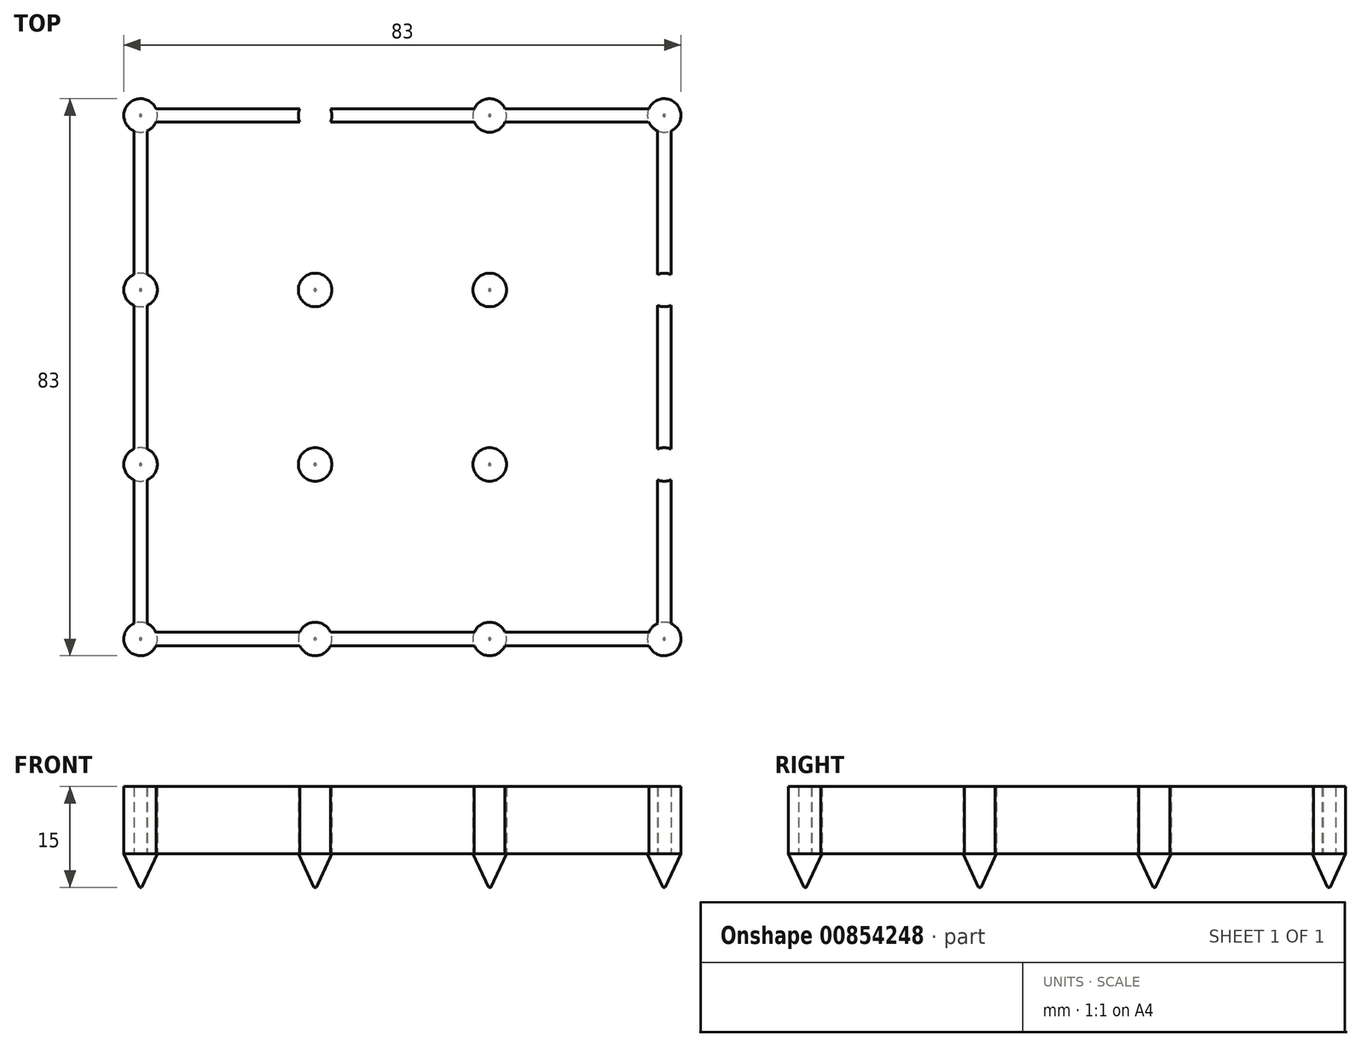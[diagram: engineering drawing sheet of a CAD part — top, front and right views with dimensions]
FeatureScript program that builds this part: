
annotation { "Feature Type Name" : "Feature", "Feature Type Description" : "" }
export const myFeature = defineFeature(function(context is Context, id is Id, definition is map)
    precondition{}
    {
        {
            var Q0;
            Q0=qCreatedBy(makeId("Top.planeOp"),FACE);
            var sketch = newSketch(context, id + "F0", { "sketchPlane" : qUnion([Q0])});
            skLineSegment(sketch, "E0.bottom", {"start": v(13, 13) * mm, "end": v(-13, 13) * mm, "construction": true});
            skLineSegment(sketch, "E0.top", {"start": v(13, -13) * mm, "end": v(-13, -13) * mm, "construction": true});
            skLineSegment(sketch, "E0.left", {"start": v(13, 13) * mm, "end": v(13, -13) * mm, "construction": true});
            skLineSegment(sketch, "E0.right", {"start": v(-13, 13) * mm, "end": v(-13, -13) * mm, "construction": true});
            skPoint(sketch, "E0.middle", {"position": v(0, 0) * mm});
            skCircle(sketch, "E1", {"center": v(13, 13) * mm, "radius": 2.5 * mm});
            skCircle(sketch, "E2", {"center": v(-13, 13) * mm, "radius": 2.5 * mm});
            skCircle(sketch, "E3", {"center": v(-13, -13) * mm, "radius": 2.5 * mm});
            skCircle(sketch, "E4", {"center": v(13, -13) * mm, "radius": 2.5 * mm});
            skLineSegment(sketch, "E5", {"start": v(-14, 10.7) * mm, "end": v(-14, -10.7) * mm});
            skLineSegment(sketch, "E6", {"start": v(-12, 10.7) * mm, "end": v(-12, -10.7) * mm});
            skLineSegment(sketch, "E7", {"start": v(-10.7, 14) * mm, "end": v(10.7, 14) * mm});
            skLineSegment(sketch, "E8", {"start": v(-10.7, 12) * mm, "end": v(10.7, 12) * mm});
            skLineSegment(sketch, "E9", {"start": v(12, 10.7) * mm, "end": v(12, -10.7) * mm});
            skLineSegment(sketch, "E10", {"start": v(14, 10.7) * mm, "end": v(14, -10.7) * mm});
            skLineSegment(sketch, "E11", {"start": v(-10.7, -12) * mm, "end": v(10.7, -12) * mm});
            skLineSegment(sketch, "E12", {"start": v(-10.7, -14) * mm, "end": v(10.7, -14) * mm});
            skLineSegment(sketch, "E13.0.1.1", {"start": v(14, 36.7) * mm, "end": v(14, 15.3) * mm});
            skLineSegment(sketch, "E13.0.1.4", {"start": v(-14, 36.7) * mm, "end": v(-14, 15.3) * mm});
            skLineSegment(sketch, "E13.0.1.5", {"start": v(13, 39) * mm, "end": v(13, 13) * mm, "construction": true});
            skLineSegment(sketch, "E13.0.1.6", {"start": v(-10.7, 40) * mm, "end": v(10.7, 40) * mm});
            skLineSegment(sketch, "E13.0.1.7", {"start": v(13, 39) * mm, "end": v(-13, 39) * mm, "construction": true});
            skLineSegment(sketch, "E13.0.1.8", {"start": v(12, 36.7) * mm, "end": v(12, 15.3) * mm});
            skLineSegment(sketch, "E13.0.1.9", {"start": v(-13, 39) * mm, "end": v(-13, 13) * mm, "construction": true});
            skLineSegment(sketch, "E13.0.1.10", {"start": v(-12, 36.7) * mm, "end": v(-12, 15.3) * mm});
            skLineSegment(sketch, "E13.0.1.11", {"start": v(-10.7, 38) * mm, "end": v(10.7, 38) * mm});
            skPoint(sketch, "E13.0.1.12", {"position": v(0, 26) * mm});
            skCircle(sketch, "E13.0.1.15", {"center": v(13, 39) * mm, "radius": 2.5 * mm});
            skCircle(sketch, "E13.0.1.16", {"center": v(-13, 39) * mm, "radius": 2.5 * mm});
            skLineSegment(sketch, "E13.1.0.0", {"start": v(15.3, -12) * mm, "end": v(36.7, -12) * mm});
            skLineSegment(sketch, "E13.1.0.1", {"start": v(40, 10.7) * mm, "end": v(40, -10.7) * mm});
            skLineSegment(sketch, "E13.1.0.2", {"start": v(15.3, -14) * mm, "end": v(36.7, -14) * mm});
            skLineSegment(sketch, "E13.1.0.3", {"start": v(39, -13) * mm, "end": v(13, -13) * mm, "construction": true});
            skLineSegment(sketch, "E13.1.0.5", {"start": v(39, 13) * mm, "end": v(39, -13) * mm, "construction": true});
            skLineSegment(sketch, "E13.1.0.6", {"start": v(15.3, 14) * mm, "end": v(36.7, 14) * mm});
            skLineSegment(sketch, "E13.1.0.7", {"start": v(39, 13) * mm, "end": v(13, 13) * mm, "construction": true});
            skLineSegment(sketch, "E13.1.0.8", {"start": v(38, 10.7) * mm, "end": v(38, -10.7) * mm});
            skLineSegment(sketch, "E13.1.0.11", {"start": v(15.3, 12) * mm, "end": v(36.7, 12) * mm});
            skPoint(sketch, "E13.1.0.12", {"position": v(26, 0) * mm});
            skCircle(sketch, "E13.1.0.14", {"center": v(39, -13) * mm, "radius": 2.5 * mm});
            skCircle(sketch, "E13.1.0.15", {"center": v(39, 13) * mm, "radius": 2.5 * mm});
            skLineSegment(sketch, "E13.1.1.0", {"start": v(15.3, 14) * mm, "end": v(36.7, 14) * mm});
            skLineSegment(sketch, "E13.1.1.1", {"start": v(40, 36.7) * mm, "end": v(40, 15.3) * mm});
            skLineSegment(sketch, "E13.1.1.2", {"start": v(15.3, 12) * mm, "end": v(36.7, 12) * mm});
            skLineSegment(sketch, "E13.1.1.3", {"start": v(39, 13) * mm, "end": v(13, 13) * mm, "construction": true});
            skLineSegment(sketch, "E13.1.1.4", {"start": v(12, 36.7) * mm, "end": v(12, 15.3) * mm});
            skLineSegment(sketch, "E13.1.1.5", {"start": v(39, 39) * mm, "end": v(39, 13) * mm, "construction": true});
            skLineSegment(sketch, "E13.1.1.6", {"start": v(15.3, 40) * mm, "end": v(36.7, 40) * mm});
            skLineSegment(sketch, "E13.1.1.7", {"start": v(39, 39) * mm, "end": v(13, 39) * mm, "construction": true});
            skLineSegment(sketch, "E13.1.1.8", {"start": v(38, 36.7) * mm, "end": v(38, 15.3) * mm});
            skLineSegment(sketch, "E13.1.1.9", {"start": v(13, 39) * mm, "end": v(13, 13) * mm, "construction": true});
            skLineSegment(sketch, "E13.1.1.10", {"start": v(14, 36.7) * mm, "end": v(14, 15.3) * mm});
            skLineSegment(sketch, "E13.1.1.11", {"start": v(15.3, 38) * mm, "end": v(36.7, 38) * mm});
            skPoint(sketch, "E13.1.1.12", {"position": v(26, 26) * mm});
            skCircle(sketch, "E13.1.1.14", {"center": v(39, 13) * mm, "radius": 2.5 * mm});
            skCircle(sketch, "E13.1.1.15", {"center": v(39, 39) * mm, "radius": 2.5 * mm});
            skCircle(sketch, "E13.1.1.16", {"center": v(13, 39) * mm, "radius": 2.5 * mm});
            skLineSegment(sketch, "E13.direction1", {"start": v(-13, -13) * mm, "end": v(13, -13) * mm, "construction": true});
            skLineSegment(sketch, "E13.direction2", {"start": v(-13, -13) * mm, "end": v(-13, 13) * mm, "construction": true});
            skLineSegment(sketch, "E14.3.0.2", {"start": v(14, 62.7) * mm, "end": v(14, 41.3) * mm});
            skLineSegment(sketch, "E14.12.0.2", {"start": v(-14, 62.7) * mm, "end": v(-14, 41.3) * mm});
            skLineSegment(sketch, "E14.15.0.2", {"start": v(13, 65) * mm, "end": v(13, 39) * mm, "construction": true});
            skLineSegment(sketch, "E14.18.0.2", {"start": v(-10.7, 66) * mm, "end": v(10.7, 66) * mm});
            skLineSegment(sketch, "E14.21.0.2", {"start": v(13, 65) * mm, "end": v(-13, 65) * mm, "construction": true});
            skLineSegment(sketch, "E14.24.0.2", {"start": v(12, 62.7) * mm, "end": v(12, 41.3) * mm});
            skLineSegment(sketch, "E14.27.0.2", {"start": v(-13, 65) * mm, "end": v(-13, 39) * mm, "construction": true});
            skLineSegment(sketch, "E14.30.0.2", {"start": v(-12, 62.7) * mm, "end": v(-12, 41.3) * mm});
            skLineSegment(sketch, "E14.33.0.2", {"start": v(-10.7, 64) * mm, "end": v(10.7, 64) * mm});
            skPoint(sketch, "E14.36.0.2", {"position": v(0, 52) * mm});
            skCircle(sketch, "E14.41.0.2", {"center": v(13, 65) * mm, "radius": 2.5 * mm});
            skCircle(sketch, "E14.43.0.2", {"center": v(-13, 65) * mm, "radius": 2.5 * mm});
            skLineSegment(sketch, "E14.3.1.2", {"start": v(40, 62.7) * mm, "end": v(40, 41.3) * mm});
            skLineSegment(sketch, "E14.12.1.2", {"start": v(12, 62.7) * mm, "end": v(12, 41.3) * mm});
            skLineSegment(sketch, "E14.15.1.2", {"start": v(39, 65) * mm, "end": v(39, 39) * mm, "construction": true});
            skLineSegment(sketch, "E14.18.1.2", {"start": v(15.3, 66) * mm, "end": v(36.7, 66) * mm});
            skLineSegment(sketch, "E14.21.1.2", {"start": v(39, 65) * mm, "end": v(13, 65) * mm, "construction": true});
            skLineSegment(sketch, "E14.24.1.2", {"start": v(38, 62.7) * mm, "end": v(38, 41.3) * mm});
            skLineSegment(sketch, "E14.27.1.2", {"start": v(13, 65) * mm, "end": v(13, 39) * mm, "construction": true});
            skLineSegment(sketch, "E14.30.1.2", {"start": v(14, 62.7) * mm, "end": v(14, 41.3) * mm});
            skLineSegment(sketch, "E14.33.1.2", {"start": v(15.3, 64) * mm, "end": v(36.7, 64) * mm});
            skPoint(sketch, "E14.36.1.2", {"position": v(26, 52) * mm});
            skCircle(sketch, "E14.41.1.2", {"center": v(39, 65) * mm, "radius": 2.5 * mm});
            skCircle(sketch, "E14.43.1.2", {"center": v(13, 65) * mm, "radius": 2.5 * mm});
            skLineSegment(sketch, "E15.0.2.0", {"start": v(41.3, -12) * mm, "end": v(62.7, -12) * mm});
            skLineSegment(sketch, "E15.3.2.0", {"start": v(66, 10.7) * mm, "end": v(66, -10.7) * mm});
            skLineSegment(sketch, "E15.6.2.0", {"start": v(41.3, -14) * mm, "end": v(62.7, -14) * mm});
            skLineSegment(sketch, "E15.9.2.0", {"start": v(65, -13) * mm, "end": v(39, -13) * mm, "construction": true});
            skLineSegment(sketch, "E15.15.2.0", {"start": v(65, 13) * mm, "end": v(65, -13) * mm, "construction": true});
            skLineSegment(sketch, "E15.18.2.0", {"start": v(41.3, 14) * mm, "end": v(62.7, 14) * mm});
            skLineSegment(sketch, "E15.21.2.0", {"start": v(65, 13) * mm, "end": v(39, 13) * mm, "construction": true});
            skLineSegment(sketch, "E15.24.2.0", {"start": v(64, 10.7) * mm, "end": v(64, -10.7) * mm});
            skLineSegment(sketch, "E15.33.2.0", {"start": v(41.3, 12) * mm, "end": v(62.7, 12) * mm});
            skPoint(sketch, "E15.36.2.0", {"position": v(52, 0) * mm});
            skCircle(sketch, "E15.39.2.0", {"center": v(65, -13) * mm, "radius": 2.5 * mm});
            skCircle(sketch, "E15.41.2.0", {"center": v(65, 13) * mm, "radius": 2.5 * mm});
            skLineSegment(sketch, "E15.0.2.1", {"start": v(41.3, 14) * mm, "end": v(62.7, 14) * mm});
            skLineSegment(sketch, "E15.3.2.1", {"start": v(66, 36.7) * mm, "end": v(66, 15.3) * mm});
            skLineSegment(sketch, "E15.6.2.1", {"start": v(41.3, 12) * mm, "end": v(62.7, 12) * mm});
            skLineSegment(sketch, "E15.9.2.1", {"start": v(65, 13) * mm, "end": v(39, 13) * mm, "construction": true});
            skLineSegment(sketch, "E15.15.2.1", {"start": v(65, 39) * mm, "end": v(65, 13) * mm, "construction": true});
            skLineSegment(sketch, "E15.18.2.1", {"start": v(41.3, 40) * mm, "end": v(62.7, 40) * mm});
            skLineSegment(sketch, "E15.21.2.1", {"start": v(65, 39) * mm, "end": v(39, 39) * mm, "construction": true});
            skLineSegment(sketch, "E15.24.2.1", {"start": v(64, 36.7) * mm, "end": v(64, 15.3) * mm});
            skLineSegment(sketch, "E15.33.2.1", {"start": v(41.3, 38) * mm, "end": v(62.7, 38) * mm});
            skPoint(sketch, "E15.36.2.1", {"position": v(52, 26) * mm});
            skCircle(sketch, "E15.39.2.1", {"center": v(65, 13) * mm, "radius": 2.5 * mm});
            skCircle(sketch, "E15.41.2.1", {"center": v(65, 39) * mm, "radius": 2.5 * mm});
            skLineSegment(sketch, "E15.0.2.2", {"start": v(41.3, 40) * mm, "end": v(62.7, 40) * mm});
            skLineSegment(sketch, "E15.3.2.2", {"start": v(66, 62.7) * mm, "end": v(66, 41.3) * mm});
            skLineSegment(sketch, "E15.6.2.2", {"start": v(41.3, 38) * mm, "end": v(62.7, 38) * mm});
            skLineSegment(sketch, "E15.9.2.2", {"start": v(65, 39) * mm, "end": v(39, 39) * mm, "construction": true});
            skLineSegment(sketch, "E15.15.2.2", {"start": v(65, 65) * mm, "end": v(65, 39) * mm, "construction": true});
            skLineSegment(sketch, "E15.18.2.2", {"start": v(41.3, 66) * mm, "end": v(62.7, 66) * mm});
            skLineSegment(sketch, "E15.21.2.2", {"start": v(65, 65) * mm, "end": v(39, 65) * mm, "construction": true});
            skLineSegment(sketch, "E15.24.2.2", {"start": v(64, 62.7) * mm, "end": v(64, 41.3) * mm});
            skLineSegment(sketch, "E15.33.2.2", {"start": v(41.3, 64) * mm, "end": v(62.7, 64) * mm});
            skPoint(sketch, "E15.36.2.2", {"position": v(52, 52) * mm});
            skCircle(sketch, "E15.39.2.2", {"center": v(65, 39) * mm, "radius": 2.5 * mm});
            skCircle(sketch, "E15.41.2.2", {"center": v(65, 65) * mm, "radius": 2.5 * mm});
            skLineSegment(sketch, "E16", {"start": v(-13, 65) * mm, "end": v(13, 39) * mm, "construction": true});
            skLineSegment(sketch, "E17", {"start": v(-12.09, 62.67) * mm, "end": v(10.67, 39.91) * mm});
            skLineSegment(sketch, "E18", {"start": v(-10.67, 64.09) * mm, "end": v(12.09, 41.33) * mm});
            skLineSegment(sketch, "E19.1.0", {"start": v(62.67, 64.09) * mm, "end": v(39.91, 41.33) * mm});
            skLineSegment(sketch, "E19.1.1", {"start": v(64.09, 62.67) * mm, "end": v(41.33, 39.91) * mm});
            skLineSegment(sketch, "E19.2.0", {"start": v(64.09, -10.67) * mm, "end": v(41.33, 12.09) * mm});
            skLineSegment(sketch, "E19.2.1", {"start": v(62.67, -12.09) * mm, "end": v(39.91, 10.67) * mm});
            skLineSegment(sketch, "E19.3.0", {"start": v(-10.67, -12.09) * mm, "end": v(12.09, 10.67) * mm});
            skLineSegment(sketch, "E19.3.1", {"start": v(-12.09, -10.67) * mm, "end": v(10.67, 12.09) * mm});
            skLineSegment(sketch, "E19.anchor1", {"start": v(26, 26) * mm, "end": v(10.67, 39.91) * mm, "construction": true});
            skLineSegment(sketch, "E19.anchor2", {"start": v(26, 26) * mm, "end": v(12.09, 10.67) * mm, "construction": true});
            skSolve(sketch);
        }
        {
            var Q0;
            {var subQ0=sQuery(id+"F0.wireOp",EDGE,"E14.43.0.2");var subQ1=makeQuery(id+"F0.imprint","INTERSECT",VERTEX,{"derivedFrom":[sQuery(id+"F0.wireOp",EDGE,"E14.12.0.2"),subQ0]});Q0=makeQuery(id+"F0.imprint","IMPRINT",FACE,{"disambiguationData":[TD([[makeQuery(id+"F0.imprint","IMPRINT",EDGE,{"disambiguationData":[TD([[subQ1,1.0]])],"derivedFrom":subQ0}),1.0]])]});}
            var Q1;
            {var subQ0=sQuery(id+"F0.wireOp",EDGE,"E13.0.1.16");var subQ5=makeQuery(id+"F0.imprint","INTERSECT",VERTEX,{"derivedFrom":[sQuery(id+"F0.wireOp",EDGE,"E13.0.1.6"),subQ0]});Q1=makeQuery(id+"F0.imprint","IMPRINT",FACE,{"disambiguationData":[TD([[makeQuery(id+"F0.imprint","IMPRINT",EDGE,{"disambiguationData":[TD([[subQ5,-1.0]])],"derivedFrom":subQ0}),1.0]])]});}
            var Q2;
            {var subQ0=sQuery(id+"F0.wireOp",EDGE,"E2");var subQ5=makeQuery(id+"F0.imprint","INTERSECT",VERTEX,{"derivedFrom":[sQuery(id+"F0.wireOp",EDGE,"E7"),subQ0]});Q2=makeQuery(id+"F0.imprint","IMPRINT",FACE,{"disambiguationData":[TD([[makeQuery(id+"F0.imprint","IMPRINT",EDGE,{"disambiguationData":[TD([[subQ5,-1.0]])],"derivedFrom":subQ0}),1.0]])]});}
            var Q3;
            {var subQ0=sQuery(id+"F0.wireOp",EDGE,"E3");var subQ1=makeQuery(id+"F0.imprint","INTERSECT",VERTEX,{"derivedFrom":[subQ0,sQuery(id+"F0.wireOp",EDGE,"E6")]});Q3=makeQuery(id+"F0.imprint","IMPRINT",FACE,{"disambiguationData":[TD([[makeQuery(id+"F0.imprint","IMPRINT",EDGE,{"disambiguationData":[TD([[subQ1,1.0]])],"derivedFrom":subQ0}),1.0]])]});}
            var Q4;
            {var subQ0=sQuery(id+"F0.wireOp",EDGE,"E14.43.1.2");var subQ4=makeQuery(id+"F0.imprint","INTERSECT",VERTEX,{"derivedFrom":[sQuery(id+"F0.wireOp",EDGE,"E14.18.0.2"),subQ0]});Q4=makeQuery(id+"F0.imprint","IMPRINT",FACE,{"disambiguationData":[TD([[makeQuery(id+"F0.imprint","IMPRINT",EDGE,{"disambiguationData":[TD([[subQ4,1.0]])],"derivedFrom":subQ0}),1.0]])]});}
            var Q5;
            {var subQ0=sQuery(id+"F0.wireOp",EDGE,"E13.0.1.15");var subQ5=makeQuery(id+"F0.imprint","INTERSECT",VERTEX,{"derivedFrom":[sQuery(id+"F0.wireOp",EDGE,"E13.1.1.6"),subQ0]});Q5=makeQuery(id+"F0.imprint","IMPRINT",FACE,{"disambiguationData":[TD([[makeQuery(id+"F0.imprint","IMPRINT",EDGE,{"disambiguationData":[TD([[subQ5,-1.0]])],"derivedFrom":subQ0}),1.0]])]});}
            var Q6;
            {var subQ0=sQuery(id+"F0.wireOp",EDGE,"E1");var subQ5=makeQuery(id+"F0.imprint","INTERSECT",VERTEX,{"derivedFrom":[sQuery(id+"F0.wireOp",EDGE,"E13.1.1.0"),subQ0]});Q6=makeQuery(id+"F0.imprint","IMPRINT",FACE,{"disambiguationData":[TD([[makeQuery(id+"F0.imprint","IMPRINT",EDGE,{"disambiguationData":[TD([[subQ5,-1.0]])],"derivedFrom":subQ0}),1.0]])]});}
            var Q7;
            {var subQ0=sQuery(id+"F0.wireOp",EDGE,"E4");var subQ5=makeQuery(id+"F0.imprint","INTERSECT",VERTEX,{"derivedFrom":[sQuery(id+"F0.wireOp",EDGE,"E13.1.0.0"),subQ0]});Q7=makeQuery(id+"F0.imprint","IMPRINT",FACE,{"disambiguationData":[TD([[makeQuery(id+"F0.imprint","IMPRINT",EDGE,{"disambiguationData":[TD([[subQ5,-1.0]])],"derivedFrom":subQ0}),1.0]])]});}
            var Q8;
            {var subQ0=sQuery(id+"F0.wireOp",EDGE,"E14.41.1.2");var subQ4=makeQuery(id+"F0.imprint","INTERSECT",VERTEX,{"derivedFrom":[sQuery(id+"F0.wireOp",EDGE,"E14.18.1.2"),subQ0]});Q8=makeQuery(id+"F0.imprint","IMPRINT",FACE,{"disambiguationData":[TD([[makeQuery(id+"F0.imprint","IMPRINT",EDGE,{"disambiguationData":[TD([[subQ4,1.0]])],"derivedFrom":subQ0}),1.0]])]});}
            var Q9;
            {var subQ0=sQuery(id+"F0.wireOp",EDGE,"E13.1.1.15");var subQ5=makeQuery(id+"F0.imprint","INTERSECT",VERTEX,{"derivedFrom":[sQuery(id+"F0.wireOp",EDGE,"E15.0.2.2"),subQ0]});Q9=makeQuery(id+"F0.imprint","IMPRINT",FACE,{"disambiguationData":[TD([[makeQuery(id+"F0.imprint","IMPRINT",EDGE,{"disambiguationData":[TD([[subQ5,-1.0]])],"derivedFrom":subQ0}),1.0]])]});}
            var Q10;
            {var subQ0=sQuery(id+"F0.wireOp",EDGE,"E13.1.0.15");var subQ5=makeQuery(id+"F0.imprint","INTERSECT",VERTEX,{"derivedFrom":[sQuery(id+"F0.wireOp",EDGE,"E15.0.2.1"),subQ0]});Q10=makeQuery(id+"F0.imprint","IMPRINT",FACE,{"disambiguationData":[TD([[makeQuery(id+"F0.imprint","IMPRINT",EDGE,{"disambiguationData":[TD([[subQ5,-1.0]])],"derivedFrom":subQ0}),1.0]])]});}
            var Q11;
            {var subQ0=sQuery(id+"F0.wireOp",EDGE,"E13.1.0.14");var subQ5=makeQuery(id+"F0.imprint","INTERSECT",VERTEX,{"derivedFrom":[sQuery(id+"F0.wireOp",EDGE,"E15.0.2.0"),subQ0]});Q11=makeQuery(id+"F0.imprint","IMPRINT",FACE,{"disambiguationData":[TD([[makeQuery(id+"F0.imprint","IMPRINT",EDGE,{"disambiguationData":[TD([[subQ5,-1.0]])],"derivedFrom":subQ0}),1.0]])]});}
            var Q12;
            {var subQ0=sQuery(id+"F0.wireOp",EDGE,"E15.41.2.2");var subQ1=makeQuery(id+"F0.imprint","INTERSECT",VERTEX,{"derivedFrom":[sQuery(id+"F0.wireOp",EDGE,"E15.18.2.2"),subQ0]});Q12=makeQuery(id+"F0.imprint","IMPRINT",FACE,{"disambiguationData":[TD([[makeQuery(id+"F0.imprint","IMPRINT",EDGE,{"disambiguationData":[TD([[subQ1,-1.0]])],"derivedFrom":subQ0}),1.0]])]});}
            var Q13;
            {var subQ0=sQuery(id+"F0.wireOp",EDGE,"E15.39.2.2");var subQ5=makeQuery(id+"F0.imprint","INTERSECT",VERTEX,{"derivedFrom":[sQuery(id+"F0.wireOp",EDGE,"E15.3.2.2"),subQ0]});Q13=makeQuery(id+"F0.imprint","IMPRINT",FACE,{"disambiguationData":[TD([[makeQuery(id+"F0.imprint","IMPRINT",EDGE,{"disambiguationData":[TD([[subQ5,-1.0]])],"derivedFrom":subQ0}),1.0]])]});}
            var Q14;
            {var subQ0=sQuery(id+"F0.wireOp",EDGE,"E15.39.2.1");var subQ5=makeQuery(id+"F0.imprint","INTERSECT",VERTEX,{"derivedFrom":[sQuery(id+"F0.wireOp",EDGE,"E15.3.2.1"),subQ0]});Q14=makeQuery(id+"F0.imprint","IMPRINT",FACE,{"disambiguationData":[TD([[makeQuery(id+"F0.imprint","IMPRINT",EDGE,{"disambiguationData":[TD([[subQ5,-1.0]])],"derivedFrom":subQ0}),1.0]])]});}
            var Q15;
            {var subQ0=sQuery(id+"F0.wireOp",EDGE,"E15.39.2.0");var subQ1=makeQuery(id+"F0.imprint","INTERSECT",VERTEX,{"derivedFrom":[sQuery(id+"F0.wireOp",EDGE,"E15.3.2.0"),subQ0]});Q15=makeQuery(id+"F0.imprint","IMPRINT",FACE,{"disambiguationData":[TD([[makeQuery(id+"F0.imprint","IMPRINT",EDGE,{"disambiguationData":[TD([[subQ1,-1.0]])],"derivedFrom":subQ0}),1.0]])]});}
            extrude(context, id + "F1", {"entities" : qUnion([Q0, Q1, Q2, Q3, Q4, Q5, Q6, Q7, Q8, Q9, Q10, Q11, Q12, Q13, Q14, Q15]), "oppositeDirection" : true, "depth" : 5 * mm, "offsetDistance" : 25 * mm, "hasDraft" : true, "draftAngle" : 25 * degree, "draftPullDirection" : true});
        }
        {
            var Q0;
            {var subQ0=sQuery(id+"F0.wireOp",EDGE,"E14.43.0.2");var subQ4=makeQuery(id+"F0.imprint","INTERSECT",VERTEX,{"derivedFrom":[sQuery(id+"F0.wireOp",EDGE,"E14.12.0.2"),subQ0]});Q0=makeQuery(id+"F0.imprint","IMPRINT",FACE,{"disambiguationData":[TD([[makeQuery(id+"F0.imprint","IMPRINT",EDGE,{"disambiguationData":[TD([[subQ4,1.0]])],"derivedFrom":subQ0}),1.0]])]});}
            var Q1;
            {var subQ1=sQuery(id+"F0.wireOp",EDGE,"E14.12.0.2");Q1=makeQuery(id+"F0.imprint","IMPRINT",FACE,{"disambiguationData":[TD([[makeQuery(id+"F0.imprint","IMPRINT",EDGE,{"derivedFrom":subQ1}),1.0]])]});}
            var Q2;
            {var subQ0=sQuery(id+"F0.wireOp",EDGE,"E13.0.1.16");var subQ5=makeQuery(id+"F0.imprint","INTERSECT",VERTEX,{"derivedFrom":[sQuery(id+"F0.wireOp",EDGE,"E13.0.1.6"),subQ0]});Q2=makeQuery(id+"F0.imprint","IMPRINT",FACE,{"disambiguationData":[TD([[makeQuery(id+"F0.imprint","IMPRINT",EDGE,{"disambiguationData":[TD([[subQ5,-1.0]])],"derivedFrom":subQ0}),1.0]])]});}
            var Q3;
            {var subQ0=sQuery(id+"F0.wireOp",EDGE,"E13.0.1.4");Q3=makeQuery(id+"F0.imprint","IMPRINT",FACE,{"disambiguationData":[TD([[makeQuery(id+"F0.imprint","IMPRINT",EDGE,{"derivedFrom":subQ0}),1.0]])]});}
            var Q4;
            {var subQ0=sQuery(id+"F0.wireOp",EDGE,"E2");var subQ5=makeQuery(id+"F0.imprint","INTERSECT",VERTEX,{"derivedFrom":[sQuery(id+"F0.wireOp",EDGE,"E7"),subQ0]});Q4=makeQuery(id+"F0.imprint","IMPRINT",FACE,{"disambiguationData":[TD([[makeQuery(id+"F0.imprint","IMPRINT",EDGE,{"disambiguationData":[TD([[subQ5,-1.0]])],"derivedFrom":subQ0}),1.0]])]});}
            var Q5;
            {var subQ1=sQuery(id+"F0.wireOp",EDGE,"E5");Q5=makeQuery(id+"F0.imprint","IMPRINT",FACE,{"disambiguationData":[TD([[makeQuery(id+"F0.imprint","IMPRINT",EDGE,{"derivedFrom":subQ1}),1.0]])]});}
            var Q6;
            {var subQ0=sQuery(id+"F0.wireOp",EDGE,"E3");var subQ4=makeQuery(id+"F0.imprint","INTERSECT",VERTEX,{"derivedFrom":[subQ0,sQuery(id+"F0.wireOp",EDGE,"E11")]});Q6=makeQuery(id+"F0.imprint","IMPRINT",FACE,{"disambiguationData":[TD([[makeQuery(id+"F0.imprint","IMPRINT",EDGE,{"disambiguationData":[TD([[subQ4,1.0]])],"derivedFrom":subQ0}),1.0]])]});}
            var Q7;
            {var subQ1=sQuery(id+"F0.wireOp",EDGE,"E14.18.0.2");Q7=makeQuery(id+"F0.imprint","IMPRINT",FACE,{"disambiguationData":[TD([[makeQuery(id+"F0.imprint","IMPRINT",EDGE,{"derivedFrom":subQ1}),-1.0]])]});}
            var Q8;
            {var subQ1=sQuery(id+"F0.wireOp",EDGE,"E13.0.1.11");Q8=makeQuery(id+"F0.imprint","IMPRINT",FACE,{"disambiguationData":[TD([[makeQuery(id+"F0.imprint","IMPRINT",EDGE,{"derivedFrom":subQ1}),1.0]])]});}
            var Q9;
            {var subQ1=sQuery(id+"F0.wireOp",EDGE,"E7");Q9=makeQuery(id+"F0.imprint","IMPRINT",FACE,{"disambiguationData":[TD([[makeQuery(id+"F0.imprint","IMPRINT",EDGE,{"derivedFrom":subQ1}),-1.0]])]});}
            var Q10;
            {var subQ3=sQuery(id+"F0.wireOp",EDGE,"E12");Q10=makeQuery(id+"F0.imprint","IMPRINT",FACE,{"disambiguationData":[TD([[makeQuery(id+"F0.imprint","IMPRINT",EDGE,{"derivedFrom":subQ3}),1.0]])]});}
            var Q11;
            {var subQ0=sQuery(id+"F0.wireOp",EDGE,"E4");var subQ5=makeQuery(id+"F0.imprint","INTERSECT",VERTEX,{"derivedFrom":[sQuery(id+"F0.wireOp",EDGE,"E13.1.0.0"),subQ0]});Q11=makeQuery(id+"F0.imprint","IMPRINT",FACE,{"disambiguationData":[TD([[makeQuery(id+"F0.imprint","IMPRINT",EDGE,{"disambiguationData":[TD([[subQ5,-1.0]])],"derivedFrom":subQ0}),1.0]])]});}
            var Q12;
            {var subQ1=sQuery(id+"F0.wireOp",EDGE,"E10");Q12=makeQuery(id+"F0.imprint","IMPRINT",FACE,{"disambiguationData":[TD([[makeQuery(id+"F0.imprint","IMPRINT",EDGE,{"derivedFrom":subQ1}),-1.0]])]});}
            var Q13;
            {var subQ0=sQuery(id+"F0.wireOp",EDGE,"E1");var subQ5=makeQuery(id+"F0.imprint","INTERSECT",VERTEX,{"derivedFrom":[sQuery(id+"F0.wireOp",EDGE,"E13.1.1.0"),subQ0]});Q13=makeQuery(id+"F0.imprint","IMPRINT",FACE,{"disambiguationData":[TD([[makeQuery(id+"F0.imprint","IMPRINT",EDGE,{"disambiguationData":[TD([[subQ5,-1.0]])],"derivedFrom":subQ0}),1.0]])]});}
            var Q14;
            {var subQ0=sQuery(id+"F0.wireOp",EDGE,"E13.1.1.4");Q14=makeQuery(id+"F0.imprint","IMPRINT",FACE,{"disambiguationData":[TD([[makeQuery(id+"F0.imprint","IMPRINT",EDGE,{"derivedFrom":subQ0}),1.0]])]});}
            var Q15;
            {var subQ0=sQuery(id+"F0.wireOp",EDGE,"E13.0.1.15");var subQ5=makeQuery(id+"F0.imprint","INTERSECT",VERTEX,{"derivedFrom":[sQuery(id+"F0.wireOp",EDGE,"E13.1.1.6"),subQ0]});Q15=makeQuery(id+"F0.imprint","IMPRINT",FACE,{"disambiguationData":[TD([[makeQuery(id+"F0.imprint","IMPRINT",EDGE,{"disambiguationData":[TD([[subQ5,-1.0]])],"derivedFrom":subQ0}),1.0]])]});}
            var Q16;
            {var subQ1=sQuery(id+"F0.wireOp",EDGE,"E14.30.1.2");Q16=makeQuery(id+"F0.imprint","IMPRINT",FACE,{"disambiguationData":[TD([[makeQuery(id+"F0.imprint","IMPRINT",EDGE,{"derivedFrom":subQ1}),-1.0]])]});}
            var Q17;
            {var subQ0=sQuery(id+"F0.wireOp",EDGE,"E14.43.1.2");var subQ4=makeQuery(id+"F0.imprint","INTERSECT",VERTEX,{"derivedFrom":[sQuery(id+"F0.wireOp",EDGE,"E14.18.0.2"),subQ0]});Q17=makeQuery(id+"F0.imprint","IMPRINT",FACE,{"disambiguationData":[TD([[makeQuery(id+"F0.imprint","IMPRINT",EDGE,{"disambiguationData":[TD([[subQ4,1.0]])],"derivedFrom":subQ0}),1.0]])]});}
            var Q18;
            {var subQ0=sQuery(id+"F0.wireOp",EDGE,"E14.18.1.2");Q18=makeQuery(id+"F0.imprint","IMPRINT",FACE,{"disambiguationData":[TD([[makeQuery(id+"F0.imprint","IMPRINT",EDGE,{"derivedFrom":subQ0}),-1.0]])]});}
            var Q19;
            {var subQ0=sQuery(id+"F0.wireOp",EDGE,"E13.1.1.6");Q19=makeQuery(id+"F0.imprint","IMPRINT",FACE,{"disambiguationData":[TD([[makeQuery(id+"F0.imprint","IMPRINT",EDGE,{"derivedFrom":subQ0}),-1.0]])]});}
            var Q20;
            {var subQ0=sQuery(id+"F0.wireOp",EDGE,"E13.1.1.0");Q20=makeQuery(id+"F0.imprint","IMPRINT",FACE,{"disambiguationData":[TD([[makeQuery(id+"F0.imprint","IMPRINT",EDGE,{"derivedFrom":subQ0}),-1.0]])]});}
            var Q21;
            {var subQ0=sQuery(id+"F0.wireOp",EDGE,"E13.1.0.0");Q21=makeQuery(id+"F0.imprint","IMPRINT",FACE,{"disambiguationData":[TD([[makeQuery(id+"F0.imprint","IMPRINT",EDGE,{"derivedFrom":subQ0}),-1.0]])]});}
            var Q22;
            {var subQ0=sQuery(id+"F0.wireOp",EDGE,"E14.41.1.2");var subQ4=makeQuery(id+"F0.imprint","INTERSECT",VERTEX,{"derivedFrom":[sQuery(id+"F0.wireOp",EDGE,"E14.18.1.2"),subQ0]});Q22=makeQuery(id+"F0.imprint","IMPRINT",FACE,{"disambiguationData":[TD([[makeQuery(id+"F0.imprint","IMPRINT",EDGE,{"disambiguationData":[TD([[subQ4,1.0]])],"derivedFrom":subQ0}),1.0]])]});}
            var Q23;
            {var subQ1=sQuery(id+"F0.wireOp",EDGE,"E14.24.1.2");Q23=makeQuery(id+"F0.imprint","IMPRINT",FACE,{"disambiguationData":[TD([[makeQuery(id+"F0.imprint","IMPRINT",EDGE,{"derivedFrom":subQ1}),1.0]])]});}
            var Q24;
            {var subQ0=sQuery(id+"F0.wireOp",EDGE,"E13.1.1.15");var subQ4=makeQuery(id+"F0.imprint","INTERSECT",VERTEX,{"derivedFrom":[sQuery(id+"F0.wireOp",EDGE,"E15.0.2.2"),subQ0]});Q24=makeQuery(id+"F0.imprint","IMPRINT",FACE,{"disambiguationData":[TD([[makeQuery(id+"F0.imprint","IMPRINT",EDGE,{"disambiguationData":[TD([[subQ4,1.0]])],"derivedFrom":subQ0}),1.0]])]});}
            var Q25;
            {var subQ0=sQuery(id+"F0.wireOp",EDGE,"E13.1.1.8");Q25=makeQuery(id+"F0.imprint","IMPRINT",FACE,{"disambiguationData":[TD([[makeQuery(id+"F0.imprint","IMPRINT",EDGE,{"derivedFrom":subQ0}),1.0]])]});}
            var Q26;
            {var subQ0=sQuery(id+"F0.wireOp",EDGE,"E13.1.0.15");var subQ5=makeQuery(id+"F0.imprint","INTERSECT",VERTEX,{"derivedFrom":[sQuery(id+"F0.wireOp",EDGE,"E15.0.2.1"),subQ0]});Q26=makeQuery(id+"F0.imprint","IMPRINT",FACE,{"disambiguationData":[TD([[makeQuery(id+"F0.imprint","IMPRINT",EDGE,{"disambiguationData":[TD([[subQ5,-1.0]])],"derivedFrom":subQ0}),1.0]])]});}
            var Q27;
            {var subQ0=sQuery(id+"F0.wireOp",EDGE,"E13.1.0.14");var subQ5=makeQuery(id+"F0.imprint","INTERSECT",VERTEX,{"derivedFrom":[sQuery(id+"F0.wireOp",EDGE,"E15.0.2.0"),subQ0]});Q27=makeQuery(id+"F0.imprint","IMPRINT",FACE,{"disambiguationData":[TD([[makeQuery(id+"F0.imprint","IMPRINT",EDGE,{"disambiguationData":[TD([[subQ5,-1.0]])],"derivedFrom":subQ0}),1.0]])]});}
            var Q28;
            {var subQ1=sQuery(id+"F0.wireOp",EDGE,"E15.18.2.2");Q28=makeQuery(id+"F0.imprint","IMPRINT",FACE,{"disambiguationData":[TD([[makeQuery(id+"F0.imprint","IMPRINT",EDGE,{"derivedFrom":subQ1}),-1.0]])]});}
            var Q29;
            {var subQ3=sQuery(id+"F0.wireOp",EDGE,"E15.6.2.2");Q29=makeQuery(id+"F0.imprint","IMPRINT",FACE,{"disambiguationData":[TD([[makeQuery(id+"F0.imprint","IMPRINT",EDGE,{"derivedFrom":subQ3}),1.0]])]});}
            var Q30;
            {var subQ1=sQuery(id+"F0.wireOp",EDGE,"E15.0.2.1");Q30=makeQuery(id+"F0.imprint","IMPRINT",FACE,{"disambiguationData":[TD([[makeQuery(id+"F0.imprint","IMPRINT",EDGE,{"derivedFrom":subQ1}),-1.0]])]});}
            var Q31;
            {var subQ1=sQuery(id+"F0.wireOp",EDGE,"E15.6.2.0");Q31=makeQuery(id+"F0.imprint","IMPRINT",FACE,{"disambiguationData":[TD([[makeQuery(id+"F0.imprint","IMPRINT",EDGE,{"derivedFrom":subQ1}),1.0]])]});}
            var Q32;
            {var subQ0=sQuery(id+"F0.wireOp",EDGE,"E15.41.2.2");var subQ5=makeQuery(id+"F0.imprint","INTERSECT",VERTEX,{"derivedFrom":[sQuery(id+"F0.wireOp",EDGE,"E15.18.2.2"),subQ0]});Q32=makeQuery(id+"F0.imprint","IMPRINT",FACE,{"disambiguationData":[TD([[makeQuery(id+"F0.imprint","IMPRINT",EDGE,{"disambiguationData":[TD([[subQ5,-1.0]])],"derivedFrom":subQ0}),1.0]])]});}
            var Q33;
            {var subQ0=sQuery(id+"F0.wireOp",EDGE,"E15.39.2.2");var subQ5=makeQuery(id+"F0.imprint","INTERSECT",VERTEX,{"derivedFrom":[sQuery(id+"F0.wireOp",EDGE,"E15.3.2.2"),subQ0]});Q33=makeQuery(id+"F0.imprint","IMPRINT",FACE,{"disambiguationData":[TD([[makeQuery(id+"F0.imprint","IMPRINT",EDGE,{"disambiguationData":[TD([[subQ5,-1.0]])],"derivedFrom":subQ0}),1.0]])]});}
            var Q34;
            {var subQ0=sQuery(id+"F0.wireOp",EDGE,"E15.39.2.1");var subQ5=makeQuery(id+"F0.imprint","INTERSECT",VERTEX,{"derivedFrom":[sQuery(id+"F0.wireOp",EDGE,"E15.3.2.1"),subQ0]});Q34=makeQuery(id+"F0.imprint","IMPRINT",FACE,{"disambiguationData":[TD([[makeQuery(id+"F0.imprint","IMPRINT",EDGE,{"disambiguationData":[TD([[subQ5,-1.0]])],"derivedFrom":subQ0}),1.0]])]});}
            var Q35;
            {var subQ0=sQuery(id+"F0.wireOp",EDGE,"E15.39.2.0");var subQ5=makeQuery(id+"F0.imprint","INTERSECT",VERTEX,{"derivedFrom":[sQuery(id+"F0.wireOp",EDGE,"E15.3.2.0"),subQ0]});Q35=makeQuery(id+"F0.imprint","IMPRINT",FACE,{"disambiguationData":[TD([[makeQuery(id+"F0.imprint","IMPRINT",EDGE,{"disambiguationData":[TD([[subQ5,-1.0]])],"derivedFrom":subQ0}),1.0]])]});}
            var Q36;
            {var subQ0=sQuery(id+"F0.wireOp",EDGE,"E15.3.2.1");Q36=makeQuery(id+"F0.imprint","IMPRINT",FACE,{"disambiguationData":[TD([[makeQuery(id+"F0.imprint","IMPRINT",EDGE,{"derivedFrom":subQ0}),-1.0]])]});}
            var Q37;
            {var subQ1=sQuery(id+"F0.wireOp",EDGE,"E15.3.2.0");Q37=makeQuery(id+"F0.imprint","IMPRINT",FACE,{"disambiguationData":[TD([[makeQuery(id+"F0.imprint","IMPRINT",EDGE,{"derivedFrom":subQ1}),-1.0]])]});}
            var Q38;
            {var subQ1=sQuery(id+"F0.wireOp",EDGE,"E13.1.0.8");Q38=makeQuery(id+"F0.imprint","IMPRINT",FACE,{"disambiguationData":[TD([[makeQuery(id+"F0.imprint","IMPRINT",EDGE,{"derivedFrom":subQ1}),1.0]])]});}
            var Q39;
            {var subQ1=sQuery(id+"F0.wireOp",EDGE,"E15.3.2.2");Q39=makeQuery(id+"F0.imprint","IMPRINT",FACE,{"disambiguationData":[TD([[makeQuery(id+"F0.imprint","IMPRINT",EDGE,{"derivedFrom":subQ1}),-1.0]])]});}
            extrude(context, id + "F2", {"entities" : qUnion([Q0, Q1, Q2, Q3, Q4, Q5, Q6, Q7, Q8, Q9, Q10, Q11, Q12, Q13, Q14, Q15, Q16, Q17, Q18, Q19, Q20, Q21, Q22, Q23, Q24, Q25, Q26, Q27, Q28, Q29, Q30, Q31, Q32, Q33, Q34, Q35, Q36, Q37, Q38, Q39]), "operationType" : NewBodyOperationType.ADD, "depth" : 10 * mm, "offsetDistance" : 25 * mm});
        }
    });
